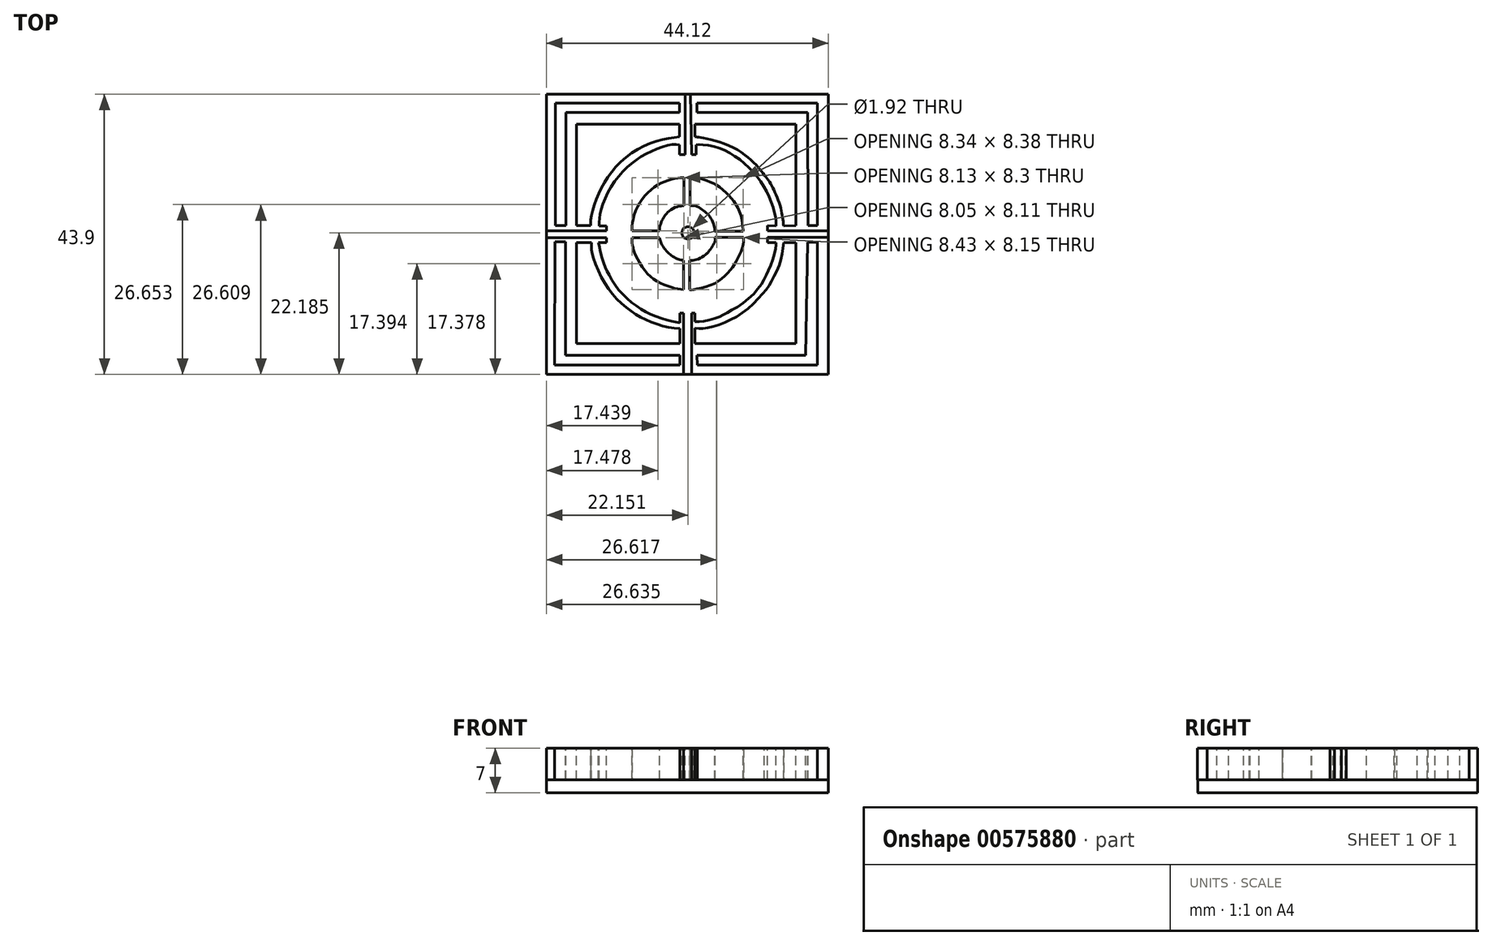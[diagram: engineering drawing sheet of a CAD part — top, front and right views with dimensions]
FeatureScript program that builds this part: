
annotation { "Feature Type Name" : "Feature", "Feature Type Description" : "" }
export const myFeature = defineFeature(function(context is Context, id is Id, definition is map)
    precondition{}
    {
        {
            var Q0;
            Q0=qCreatedBy(makeId("Top.planeOp"),FACE);
            var sketch = newSketch(context, id + "F0", { "sketchPlane" : qUnion([Q0])});
            skFitSpline(sketch, "E0", {"points": [v(14.8, 62.13) * mm, v(14.75, 42.86) * mm], "startDerivative": vector(-0.06, -19.27) * mm, "endDerivative": vector(-0.06, -19.27) * mm});
            skFitSpline(sketch, "E1", {"points": [v(14.75, 42.86) * mm, v(34.33, 42.86) * mm], "startDerivative": vector(19.6, 0) * mm, "endDerivative": vector(19.6, 0) * mm});
            skFitSpline(sketch, "E2", {"points": [v(34.33, 42.86) * mm, v(34.33, 44.38) * mm], "startDerivative": vector(0, 1.53) * mm, "endDerivative": vector(0, 1.53) * mm});
            skFitSpline(sketch, "E3", {"points": [v(34.33, 44.38) * mm, v(16.42, 44.38) * mm], "startDerivative": vector(-17.93, 0) * mm, "endDerivative": vector(-17.93, 0) * mm});
            skFitSpline(sketch, "E4", {"points": [v(16.42, 44.38) * mm, v(16.42, 62.13) * mm], "startDerivative": vector(0, 17.74) * mm, "endDerivative": vector(0, 17.74) * mm});
            skFitSpline(sketch, "E5", {"points": [v(16.42, 62.13) * mm, v(14.8, 62.13) * mm], "startDerivative": vector(-1.62, 0) * mm, "endDerivative": vector(-1.62, 0) * mm});
            skFitSpline(sketch, "E6", {"points": [v(34.33, 50.96) * mm, v(34.33, 46.2) * mm], "startDerivative": vector(0, -4.75) * mm, "endDerivative": vector(0, -4.75) * mm});
            skFitSpline(sketch, "E7", {"points": [v(34.33, 50.96) * mm, v(36.66, 50.96) * mm], "startDerivative": vector(2.34, 0) * mm, "endDerivative": vector(2.34, 0) * mm});
            skFitSpline(sketch, "E8", {"points": [v(36.66, 50.96) * mm, v(36.66, 46.2) * mm], "startDerivative": vector(0, -4.75) * mm, "endDerivative": vector(0, -4.75) * mm});
            skFitSpline(sketch, "E9", {"points": [v(34.93, 41.37) * mm, v(36.2, 41.34) * mm], "startDerivative": vector(1.22, -0.03) * mm, "endDerivative": vector(1.22, -0.03) * mm});
            skFitSpline(sketch, "E10", {"points": [v(36.2, 41.34) * mm, v(36.2, 50.96) * mm], "startDerivative": vector(0, 9.62) * mm, "endDerivative": vector(0, 9.62) * mm});
            skFitSpline(sketch, "E11", {"points": [v(34.93, 41.37) * mm, v(34.93, 50.96) * mm], "startDerivative": vector(0, 9.6) * mm, "endDerivative": vector(0, 9.6) * mm});
            skFitSpline(sketch, "E12", {"points": [v(34.33, 49.46) * mm, v(33.12, 49.7) * mm, v(30.97, 50.3) * mm, v(28.74, 51.3) * mm, v(26.75, 52.67) * mm, v(24.79, 54.57) * mm, v(23.3, 56.84) * mm, v(22.67, 58.18) * mm, v(22.03, 60.1) * mm, v(21.6, 62) * mm, v(21.6, 62.01) * mm], "startDerivative": vector(-13.94, 2.4) * mm, "endDerivative": vector(0.26, 5.24) * mm});
            skFitSpline(sketch, "E13", {"points": [v(36.66, 48.6) * mm, v(38.29, 48.6) * mm, v(41.1, 49.37) * mm, v(44.58, 51.33) * mm, v(47.54, 54.27) * mm, v(48.82, 56.2) * mm, v(50.1, 59.12) * mm, v(50.59, 62.01) * mm], "startDerivative": vector(14.49, -1.02) * mm, "endDerivative": vector(1.9, 21.32) * mm});
            skFitSpline(sketch, "E14", {"points": [v(50.59, 62.01) * mm, v(49.36, 62.01) * mm], "startDerivative": vector(-1.25, 0) * mm, "endDerivative": vector(-1.25, 0) * mm});
            skFitSpline(sketch, "E15", {"points": [v(49.36, 62.01) * mm, v(49.36, 61.46) * mm, v(48.89, 59.4) * mm, v(47.94, 57.1) * mm, v(46.93, 55.26) * mm, v(44.59, 52.79) * mm, v(41.9, 51.12) * mm, v(40.57, 50.4) * mm, v(38.37, 49.72) * mm, v(36.66, 49.61) * mm], "startDerivative": vector(0.7, -10.36) * mm, "endDerivative": vector(-15.94, 0) * mm});
            skFitSpline(sketch, "E16", {"points": [v(50.59, 64.63) * mm, v(50.2, 67.1) * mm, v(48.89, 70.6) * mm, v(47.55, 72.58) * mm], "startDerivative": vector(-0.92, 7.67) * mm, "endDerivative": vector(-5.43, 6.35) * mm});
            skFitSpline(sketch, "E17", {"points": [v(47.55, 72.58) * mm, v(46.33, 74.1) * mm, v(42.46, 77) * mm, v(37.58, 78.46) * mm, v(36.87, 78.55) * mm], "startDerivative": vector(-4.95, 6.76) * mm, "endDerivative": vector(-4.27, 0.3) * mm});
            skFitSpline(sketch, "E18", {"points": [v(36.87, 78.55) * mm, v(36.87, 77.33) * mm], "startDerivative": vector(0, -1.08) * mm, "endDerivative": vector(0, -1.08) * mm});
            skFitSpline(sketch, "E19", {"points": [v(36.87, 77.33) * mm, v(37.6, 77.33) * mm, v(39.73, 77.05) * mm, v(42.02, 76.13) * mm, v(44.29, 74.55) * mm, v(46.26, 72.58) * mm, v(47.74, 70.32) * mm, v(48.72, 68.07) * mm, v(49.31, 66.05) * mm, v(49.38, 64.63) * mm], "startDerivative": vector(9.67, 0.58) * mm, "endDerivative": vector(-0.3, -15.03) * mm});
            skFitSpline(sketch, "E20", {"points": [v(49.38, 64.63) * mm, v(50.59, 64.63) * mm], "startDerivative": vector(1.24, 0) * mm, "endDerivative": vector(1.24, 0) * mm});
            skFitSpline(sketch, "E21", {"points": [v(34.3, 77.33) * mm, v(32.9, 77.33) * mm, v(29.97, 76.37) * mm, v(27.17, 74.7) * mm, v(24.52, 72.11) * mm, v(22.5, 68.62) * mm, v(21.8, 66.05) * mm, v(21.69, 64.63) * mm], "startDerivative": vector(-12.77, 1.45) * mm, "endDerivative": vector(-0.42, -12.91) * mm});
            skFitSpline(sketch, "E22", {"points": [v(21.69, 64.63) * mm, v(20.38, 64.63) * mm], "startDerivative": vector(-1.3, 0) * mm, "endDerivative": vector(-1.3, 0) * mm});
            skFitSpline(sketch, "E23", {"points": [v(20.38, 64.63) * mm, v(20.38, 65.43) * mm, v(21.02, 68.16) * mm, v(22.78, 71.84) * mm, v(25.97, 75.45) * mm, v(30.6, 77.89) * mm, v(34.3, 78.55) * mm], "startDerivative": vector(-0.6, 8.43) * mm, "endDerivative": vector(20.4, 2.18) * mm});
            skFitSpline(sketch, "E24", {"points": [v(34.3, 78.55) * mm, v(34.3, 77.33) * mm], "startDerivative": vector(0, -1.08) * mm, "endDerivative": vector(0, -1.08) * mm});
            skFitSpline(sketch, "E25", {"points": [v(22.84, 63.84) * mm, v(22.86, 62.77) * mm], "startDerivative": vector(0.02, -1.07) * mm, "endDerivative": vector(0.02, -1.07) * mm});
            skFitSpline(sketch, "E26", {"points": [v(22.86, 62.77) * mm, v(13.46, 62.77) * mm], "startDerivative": vector(-9.4, 0) * mm, "endDerivative": vector(-9.4, 0) * mm});
            skFitSpline(sketch, "E27", {"points": [v(13.46, 62.77) * mm, v(13.46, 63.84) * mm], "startDerivative": vector(0, 1.07) * mm, "endDerivative": vector(0, 1.07) * mm});
            skFitSpline(sketch, "E28", {"points": [v(13.46, 63.84) * mm, v(22.84, 63.84) * mm], "startDerivative": vector(9.38, 0) * mm, "endDerivative": vector(9.38, 0) * mm});
            skFitSpline(sketch, "E29", {"points": [v(34.93, 52.6) * mm, v(35.89, 52.6) * mm], "startDerivative": vector(0.94, 0) * mm, "endDerivative": vector(0.94, 0) * mm});
            skFitSpline(sketch, "E30", {"points": [v(35.89, 52.6) * mm, v(35.89, 59.23) * mm], "startDerivative": vector(-0.02, 6.18) * mm, "endDerivative": vector(0, 6.62) * mm});
            skFitSpline(sketch, "E31", {"points": [v(34.93, 52.6) * mm, v(34.93, 59.23) * mm], "startDerivative": vector(0, 6.62) * mm, "endDerivative": vector(0, 6.62) * mm});
            skFitSpline(sketch, "E32", {"points": [v(34.93, 59.23) * mm, v(34.04, 59.42) * mm, v(32.96, 60) * mm, v(31.97, 61) * mm, v(31.28, 62.26) * mm, v(31.18, 62.77) * mm], "startDerivative": vector(-4.92, 0.65) * mm, "endDerivative": vector(-0.36, 3.26) * mm});
            skFitSpline(sketch, "E33", {"points": [v(31.18, 62.77) * mm, v(24.72, 62.77) * mm], "startDerivative": vector(-6.45, 0) * mm, "endDerivative": vector(-6.45, 0) * mm});
            skFitSpline(sketch, "E34", {"points": [v(24.72, 62.77) * mm, v(24.72, 63.84) * mm], "startDerivative": vector(0, 1.07) * mm, "endDerivative": vector(0, 1.07) * mm});
            skFitSpline(sketch, "E35", {"points": [v(24.72, 63.84) * mm, v(31.18, 63.84) * mm], "startDerivative": vector(6.45, 0) * mm, "endDerivative": vector(6.45, 0) * mm});
            skFitSpline(sketch, "E36", {"points": [v(35, 67.78) * mm, v(35, 74.22) * mm], "startDerivative": vector(0, 6.24) * mm, "endDerivative": vector(0, 6.24) * mm});
            skFitSpline(sketch, "E37", {"points": [v(35, 74.22) * mm, v(35.9, 74.22) * mm], "startDerivative": vector(0.93, 0) * mm, "endDerivative": vector(0.93, 0) * mm});
            skFitSpline(sketch, "E38", {"points": [v(35.9, 74.22) * mm, v(35.9, 67.78) * mm], "startDerivative": vector(0, -6.44) * mm, "endDerivative": vector(0, -6.44) * mm});
            skFitSpline(sketch, "E39", {"points": [v(31.18, 63.84) * mm, v(31.18, 64.43) * mm, v(31.6, 65.57) * mm, v(32.05, 66.33) * mm, v(33.27, 67.37) * mm, v(34.72, 67.78) * mm, v(35, 67.78) * mm], "startDerivative": vector(-0.5, 4.04) * mm, "endDerivative": vector(2.43, -0.15) * mm});
            skCircle(sketch, "E40", {"center": v(35.61, 63.53) * mm, "radius": 0.96 * mm});
            skFitSpline(sketch, "E41", {"points": [v(35.9, 67.78) * mm, v(36.73, 67.78) * mm, v(38.04, 67) * mm, v(38.94, 66.2) * mm, v(39.68, 64.68) * mm, v(39.83, 63.76) * mm], "startDerivative": vector(4.4, 0.01) * mm, "endDerivative": vector(0.37, -4.81) * mm});
            skFitSpline(sketch, "E42", {"points": [v(39.83, 63.76) * mm, v(46.25, 63.76) * mm], "startDerivative": vector(6.42, 0) * mm, "endDerivative": vector(6.42, 0) * mm});
            skFitSpline(sketch, "E43", {"points": [v(46.25, 63.76) * mm, v(46.25, 62.8) * mm], "startDerivative": vector(0, -0.95) * mm, "endDerivative": vector(0, -0.95) * mm});
            skFitSpline(sketch, "E44", {"points": [v(46.25, 62.8) * mm, v(39.83, 62.8) * mm], "startDerivative": vector(-6.42, 0) * mm, "endDerivative": vector(-6.42, 0) * mm});
            skFitSpline(sketch, "E45", {"points": [v(39.83, 62.8) * mm, v(39.83, 62.24) * mm, v(39.23, 61.11) * mm, v(38.13, 59.92) * mm, v(36.44, 59.2) * mm, v(35.89, 59.23) * mm], "startDerivative": vector(0.54, -3.65) * mm, "endDerivative": vector(-3.18, 0.59) * mm});
            skFitSpline(sketch, "E46", {"points": [v(44.3, 62.8) * mm, v(44.3, 62.07) * mm, v(43.78, 60.32) * mm, v(42.9, 58.64) * mm, v(41.5, 56.9) * mm, v(39.16, 55.34) * mm, v(36.44, 54.64) * mm, v(35.88, 54.66) * mm], "startDerivative": vector(0.66, -7) * mm, "endDerivative": vector(-5.02, 2.93) * mm});
            skFitSpline(sketch, "E47", {"points": [v(34.93, 54.66) * mm, v(33.75, 54.81) * mm, v(32.03, 55.34) * mm, v(30.18, 56.31) * mm, v(28.6, 57.96) * mm, v(27.35, 60.14) * mm, v(27.08, 60.97) * mm, v(26.87, 61.97) * mm, v(26.87, 62.77) * mm], "startDerivative": vector(-10.11, 0.86) * mm, "endDerivative": vector(0.5, 8.43) * mm});
            skFitSpline(sketch, "E48", {"points": [v(26.87, 63.84) * mm, v(26.87, 64.85) * mm, v(27.59, 67.38) * mm, v(29.28, 69.79) * mm, v(31.33, 71.28) * mm, v(33.2, 71.95) * mm, v(34.59, 72.2) * mm, v(35, 72.14) * mm], "startDerivative": vector(-0.6, 8.13) * mm, "endDerivative": vector(5.04, -1.27) * mm});
            skFitSpline(sketch, "E49", {"points": [v(35.9, 72.14) * mm, v(37.17, 72.14) * mm, v(38.93, 71.54) * mm, v(40.3, 70.85) * mm, v(41.95, 69.44) * mm, v(43.06, 68.02) * mm, v(43.97, 66.02) * mm, v(44.2, 64.3) * mm, v(44.25, 63.76) * mm], "startDerivative": vector(10.83, 1.07) * mm, "endDerivative": vector(0.71, -6.4) * mm});
            skFitSpline(sketch, "E50", {"points": [v(36.66, 46.2) * mm, v(52.53, 46.2) * mm], "startDerivative": vector(15.86, 0) * mm, "endDerivative": vector(15.86, 0) * mm});
            skFitSpline(sketch, "E51", {"points": [v(52.53, 46.2) * mm, v(52.53, 62.01) * mm], "startDerivative": vector(0, 15.8) * mm, "endDerivative": vector(0, 15.8) * mm});
            skFitSpline(sketch, "E52", {"points": [v(52.53, 62.01) * mm, v(50.59, 62.01) * mm], "startDerivative": vector(-1.96, 0) * mm, "endDerivative": vector(-1.95, 0.01) * mm});
            skFitSpline(sketch, "E53", {"points": [v(52.53, 64.67) * mm, v(50.59, 64.63) * mm], "startDerivative": vector(-1.94, -0.05) * mm, "endDerivative": vector(-1.94, -0.05) * mm});
            skFitSpline(sketch, "E54", {"points": [v(52.53, 64.67) * mm, v(52.53, 80.54) * mm], "startDerivative": vector(0, 15.87) * mm, "endDerivative": vector(0, 15.87) * mm});
            skFitSpline(sketch, "E55", {"points": [v(52.53, 80.54) * mm, v(36.66, 80.54) * mm], "startDerivative": vector(-15.86, 0) * mm, "endDerivative": vector(-15.86, 0) * mm});
            skFitSpline(sketch, "E56", {"points": [v(36.66, 80.54) * mm, v(36.66, 78.55) * mm], "startDerivative": vector(0, -2) * mm, "endDerivative": vector(0, -2) * mm});
            skFitSpline(sketch, "E57", {"points": [v(36.66, 78.55) * mm, v(36.87, 78.55) * mm], "startDerivative": vector(0.18, 0) * mm, "endDerivative": vector(0.18, 0) * mm});
            skFitSpline(sketch, "E58", {"points": [v(34.3, 80.54) * mm, v(34.3, 78.55) * mm], "startDerivative": vector(0, -2) * mm, "endDerivative": vector(0, -2) * mm});
            skFitSpline(sketch, "E59", {"points": [v(34.3, 80.54) * mm, v(18.15, 80.54) * mm], "startDerivative": vector(-16.15, 0) * mm, "endDerivative": vector(-16.15, 0) * mm});
            skFitSpline(sketch, "E60", {"points": [v(18.15, 80.54) * mm, v(18.15, 64.67) * mm], "startDerivative": vector(0, -15.87) * mm, "endDerivative": vector(0, -15.87) * mm});
            skFitSpline(sketch, "E61", {"points": [v(18.15, 64.67) * mm, v(20.38, 64.67) * mm], "startDerivative": vector(2.22, 0) * mm, "endDerivative": vector(2.22, 0) * mm});
            skFitSpline(sketch, "E62", {"points": [v(21.69, 64.63) * mm, v(22.84, 64.63) * mm], "startDerivative": vector(1.15, 0) * mm, "endDerivative": vector(1.15, 0) * mm});
            skFitSpline(sketch, "E63", {"points": [v(22.84, 64.63) * mm, v(22.84, 63.84) * mm], "startDerivative": vector(0, -0.78) * mm, "endDerivative": vector(0, -0.78) * mm});
            skFitSpline(sketch, "E64", {"points": [v(22.86, 62.77) * mm, v(22.86, 62.01) * mm], "startDerivative": vector(0, -0.76) * mm, "endDerivative": vector(0, -0.76) * mm});
            skFitSpline(sketch, "E65", {"points": [v(22.86, 62.01) * mm, v(21.6, 62) * mm], "startDerivative": vector(-1.25, -0.01) * mm, "endDerivative": vector(-1.25, -0.01) * mm});
            skFitSpline(sketch, "E66", {"points": [v(20.49, 62.03) * mm, v(18.15, 62.03) * mm], "startDerivative": vector(-2.38, 0) * mm, "endDerivative": vector(-2.38, 0) * mm});
            skFitSpline(sketch, "E67", {"points": [v(36.87, 77.33) * mm, v(36.87, 75.77) * mm], "startDerivative": vector(0, -1.7) * mm, "endDerivative": vector(0, -1.7) * mm});
            skFitSpline(sketch, "E68", {"points": [v(36.87, 75.77) * mm, v(34.3, 75.77) * mm], "startDerivative": vector(-2.56, 0) * mm, "endDerivative": vector(-2.56, 0) * mm});
            skFitSpline(sketch, "E69", {"points": [v(34.3, 75.77) * mm, v(34.3, 77.33) * mm], "startDerivative": vector(0, 1.7) * mm, "endDerivative": vector(0, 1.7) * mm});
            skFitSpline(sketch, "E70", {"points": [v(49.36, 62.01) * mm, v(48.04, 62.01) * mm], "startDerivative": vector(-1.33, 0) * mm, "endDerivative": vector(-1.33, 0) * mm});
            skFitSpline(sketch, "E71", {"points": [v(48.04, 62.01) * mm, v(48.04, 64.67) * mm], "startDerivative": vector(0, 2.41) * mm, "endDerivative": vector(0, 2.41) * mm});
            skFitSpline(sketch, "E72", {"points": [v(48.04, 64.67) * mm, v(49.38, 64.63) * mm], "startDerivative": vector(1.34, -0.05) * mm, "endDerivative": vector(1.34, -0.05) * mm});
            skFitSpline(sketch, "E73", {"points": [v(18.15, 62.03) * mm, v(18.15, 46.2) * mm], "startDerivative": vector(0, -15.81) * mm, "endDerivative": vector(0, -15.81) * mm});
            skFitSpline(sketch, "E74", {"points": [v(18.15, 46.2) * mm, v(34.33, 46.2) * mm], "startDerivative": vector(16.2, 0) * mm, "endDerivative": vector(16.2, 0) * mm});
            skFitSpline(sketch, "E75", {"points": [v(48.04, 63.87) * mm, v(57.58, 63.87) * mm], "startDerivative": vector(9.55, 0) * mm, "endDerivative": vector(9.55, 0) * mm});
            skFitSpline(sketch, "E76", {"points": [v(57.58, 63.87) * mm, v(57.58, 62.8) * mm], "startDerivative": vector(0, -1.06) * mm, "endDerivative": vector(0, -1.06) * mm});
            skFitSpline(sketch, "E77", {"points": [v(57.58, 62.8) * mm, v(48.04, 62.8) * mm], "startDerivative": vector(-9.55, 0) * mm, "endDerivative": vector(-9.55, 0) * mm});
            skFitSpline(sketch, "E78", {"points": [v(36.16, 75.77) * mm, v(36.02, 85.24) * mm], "startDerivative": vector(-0.15, 9.46) * mm, "endDerivative": vector(-0.15, 9.46) * mm});
            skFitSpline(sketch, "E79", {"points": [v(36.02, 85.24) * mm, v(35.16, 85.24) * mm], "startDerivative": vector(-0.85, 0) * mm, "endDerivative": vector(-0.85, 0) * mm});
            skFitSpline(sketch, "E80", {"points": [v(35.16, 85.24) * mm, v(35.16, 75.77) * mm], "startDerivative": vector(0, -9.46) * mm, "endDerivative": vector(0, -9.46) * mm});
            skFitSpline(sketch, "E81", {"points": [v(37.01, 44.38) * mm, v(37.04, 42.86) * mm], "startDerivative": vector(0.03, -1.53) * mm, "endDerivative": vector(0.03, -1.53) * mm});
            skFitSpline(sketch, "E82", {"points": [v(37.04, 42.86) * mm, v(55.9, 42.86) * mm], "startDerivative": vector(18.85, 0) * mm, "endDerivative": vector(18.85, 0) * mm});
            skFitSpline(sketch, "E83", {"points": [v(55.9, 42.86) * mm, v(55.9, 62.09) * mm], "startDerivative": vector(0, 19.23) * mm, "endDerivative": vector(0, 19.23) * mm});
            skFitSpline(sketch, "E84", {"points": [v(55.9, 62.09) * mm, v(54.34, 62.09) * mm], "startDerivative": vector(-1.56, 0) * mm, "endDerivative": vector(-1.56, 0) * mm});
            skFitSpline(sketch, "E85", {"points": [v(54.34, 62.09) * mm, v(54.02, 44.38) * mm], "startDerivative": vector(-0.32, -17.7) * mm, "endDerivative": vector(-0.32, -17.7) * mm});
            skFitSpline(sketch, "E86", {"points": [v(54.02, 44.38) * mm, v(37.01, 44.38) * mm], "startDerivative": vector(-17, 0) * mm, "endDerivative": vector(-17, 0) * mm});
            skFitSpline(sketch, "E87", {"points": [v(54.4, 64.64) * mm, v(55.89, 64.66) * mm], "startDerivative": vector(1.49, 0.02) * mm, "endDerivative": vector(1.49, 0.02) * mm});
            skFitSpline(sketch, "E88", {"points": [v(55.89, 64.66) * mm, v(55.89, 83.84) * mm], "startDerivative": vector(0, 19.18) * mm, "endDerivative": vector(0, 19.18) * mm});
            skFitSpline(sketch, "E89", {"points": [v(55.89, 83.84) * mm, v(37.02, 83.84) * mm], "startDerivative": vector(-18.87, 0) * mm, "endDerivative": vector(-18.87, 0) * mm});
            skFitSpline(sketch, "E90", {"points": [v(37.02, 83.84) * mm, v(37.02, 82.38) * mm], "startDerivative": vector(0, -1.46) * mm, "endDerivative": vector(0, -1.46) * mm});
            skFitSpline(sketch, "E91", {"points": [v(37.02, 82.38) * mm, v(54.34, 82.38) * mm], "startDerivative": vector(17.31, 0) * mm, "endDerivative": vector(17.31, 0) * mm});
            skFitSpline(sketch, "E92", {"points": [v(54.34, 82.38) * mm, v(54.4, 64.64) * mm], "startDerivative": vector(0.07, -17.74) * mm, "endDerivative": vector(0.07, -17.74) * mm});
            skFitSpline(sketch, "E93", {"points": [v(34.3, 82.38) * mm, v(34.25, 83.84) * mm], "startDerivative": vector(-0.04, 1.46) * mm, "endDerivative": vector(-0.04, 1.46) * mm});
            skFitSpline(sketch, "E94", {"points": [v(34.25, 83.84) * mm, v(14.82, 83.84) * mm], "startDerivative": vector(-19.43, 0) * mm, "endDerivative": vector(-19.43, 0) * mm});
            skFitSpline(sketch, "E95", {"points": [v(14.82, 83.84) * mm, v(14.82, 64.64) * mm], "startDerivative": vector(0, -19.2) * mm, "endDerivative": vector(0, -19.2) * mm});
            skFitSpline(sketch, "E96", {"points": [v(14.82, 64.64) * mm, v(16.48, 64.64) * mm], "startDerivative": vector(1.66, 0) * mm, "endDerivative": vector(1.66, 0) * mm});
            skFitSpline(sketch, "E97", {"points": [v(16.48, 64.64) * mm, v(16.48, 82.38) * mm], "startDerivative": vector(0, 17.74) * mm, "endDerivative": vector(0, 17.74) * mm});
            skFitSpline(sketch, "E98", {"points": [v(16.48, 82.38) * mm, v(34.3, 82.38) * mm], "startDerivative": vector(17.82, 0) * mm, "endDerivative": vector(17.82, 0) * mm});
            skFitSpline(sketch, "E99", {"points": [v(20.49, 62.03) * mm, v(21.6, 62) * mm], "startDerivative": vector(1.07, -0.02) * mm, "endDerivative": vector(1.07, -0.02) * mm});
            skFitSpline(sketch, "E100", {"points": [v(20.49, 62.03) * mm, v(20.49, 60.94) * mm, v(20.87, 59.43) * mm, v(22.36, 56) * mm, v(24.45, 53.2) * mm, v(26.8, 51.22) * mm, v(28.98, 49.93) * mm, v(31.78, 48.92) * mm, v(34.33, 48.55) * mm], "startDerivative": vector(-0.68, -13.26) * mm, "endDerivative": vector(19.93, -1.96) * mm});
            skSolve(sketch);
        }
        {
            var Q0;
            Q0=makeQuery(id+"F0.imprint","IMPRINT",FACE,{"disambiguationData":[TD([[makeQuery(id+"F0.imprint","IMPRINT",EDGE,{"derivedFrom":sQuery(id+"F0.wireOp",EDGE,"E0")}),1.0]])]});
            var Q1;
            Q1=makeQuery(id+"F0.imprint","IMPRINT",FACE,{"disambiguationData":[TD([[makeQuery(id+"F0.imprint","IMPRINT",EDGE,{"derivedFrom":sQuery(id+"F0.wireOp",EDGE,"E81")}),1.0]])]});
            var Q2;
            Q2=makeQuery(id+"F0.imprint","IMPRINT",FACE,{"disambiguationData":[TD([[makeQuery(id+"F0.imprint","IMPRINT",EDGE,{"derivedFrom":sQuery(id+"F0.wireOp",EDGE,"E87")}),1.0]])]});
            var Q3;
            Q3=makeQuery(id+"F0.imprint","IMPRINT",FACE,{"disambiguationData":[TD([[makeQuery(id+"F0.imprint","IMPRINT",EDGE,{"derivedFrom":sQuery(id+"F0.wireOp",EDGE,"E93")}),1.0]])]});
            var Q4;
            Q4=makeQuery(id+"F0.imprint","IMPRINT",FACE,{"disambiguationData":[TD([[makeQuery(id+"F0.imprint","IMPRINT",EDGE,{"derivedFrom":sQuery(id+"F0.wireOp",EDGE,"E66")}),1.0]])]});
            var Q5;
            Q5=makeQuery(id+"F0.imprint","IMPRINT",FACE,{"disambiguationData":[TD([[makeQuery(id+"F0.imprint","IMPRINT",EDGE,{"derivedFrom":sQuery(id+"F0.wireOp",EDGE,"E9")}),1.0]])]});
            var Q6;
            {var subQ0=sQuery(id+"F0.wireOp",EDGE,"E50");Q6=makeQuery(id+"F0.imprint","IMPRINT",FACE,{"disambiguationData":[TD([[makeQuery(id+"F0.imprint","IMPRINT",EDGE,{"derivedFrom":subQ0}),1.0]])]});}
            var Q7;
            Q7=makeQuery(id+"F0.imprint","IMPRINT",FACE,{"disambiguationData":[TD([[makeQuery(id+"F0.imprint","IMPRINT",EDGE,{"derivedFrom":sQuery(id+"F0.wireOp",EDGE,"E16")}),-1.0]])]});
            var Q8;
            {var subQ0=sQuery(id+"F0.wireOp",EDGE,"E58");Q8=makeQuery(id+"F0.imprint","IMPRINT",FACE,{"disambiguationData":[TD([[makeQuery(id+"F0.imprint","IMPRINT",EDGE,{"derivedFrom":subQ0}),-1.0]])]});}
            var Q9;
            Q9=makeQuery(id+"F0.imprint","IMPRINT",FACE,{"disambiguationData":[TD([[makeQuery(id+"F0.imprint","IMPRINT",EDGE,{"derivedFrom":sQuery(id+"F0.wireOp",EDGE,"E25")}),-1.0]])]});
            var Q10;
            {var subQ0=sQuery(id+"F0.wireOp",EDGE,"E78");Q10=makeQuery(id+"F0.imprint","IMPRINT",FACE,{"disambiguationData":[TD([[makeQuery(id+"F0.imprint","IMPRINT",EDGE,{"derivedFrom":subQ0}),1.0]])]});}
            var Q11;
            {var subQ0=sQuery(id+"F0.wireOp",EDGE,"E75");Q11=makeQuery(id+"F0.imprint","IMPRINT",FACE,{"disambiguationData":[TD([[makeQuery(id+"F0.imprint","IMPRINT",EDGE,{"derivedFrom":subQ0}),-1.0]])]});}
            var Q12;
            {var subQ7=sQuery(id+"F0.wireOp",EDGE,"E15");Q12=makeQuery(id+"F0.imprint","IMPRINT",FACE,{"disambiguationData":[TD([[makeQuery(id+"F0.imprint","IMPRINT",EDGE,{"derivedFrom":subQ7}),-1.0]])]});}
            var Q13;
            {var subQ15=sQuery(id+"F0.wireOp",EDGE,"E29");Q13=makeQuery(id+"F0.imprint","IMPRINT",FACE,{"disambiguationData":[TD([[makeQuery(id+"F0.imprint","IMPRINT",EDGE,{"derivedFrom":subQ15}),1.0]])]});}
            extrude(context, id + "F1", {"entities" : qUnion([Q0, Q1, Q2, Q3, Q4, Q5, Q6, Q7, Q8, Q9, Q10, Q11, Q12, Q13]), "oppositeDirection" : true, "depth" : 5 * mm, "offsetDistance" : 25 * mm});
        }
        {
            var Q0;
            Q0=makeQuery(id+"F1.opExtrude","CAP_FACE",FACE,{"disambiguationData":[OSD([sQuery(id+"F0.wireOp",EDGE,"E6"),sQuery(id+"F0.wireOp",EDGE,"E7"),sQuery(id+"F0.wireOp",EDGE,"E8"),sQuery(id+"F0.wireOp",EDGE,"E9"),sQuery(id+"F0.wireOp",EDGE,"E10"),sQuery(id+"F0.wireOp",EDGE,"E11"),sQuery(id+"F0.wireOp",EDGE,"E13"),sQuery(id+"F0.wireOp",EDGE,"E14"),sQuery(id+"F0.wireOp",EDGE,"E18"),sQuery(id+"F0.wireOp",EDGE,"E20"),sQuery(id+"F0.wireOp",EDGE,"E22"),sQuery(id+"F0.wireOp",EDGE,"E23"),sQuery(id+"F0.wireOp",EDGE,"E24"),sQuery(id+"F0.wireOp",EDGE,"E26"),sQuery(id+"F0.wireOp",EDGE,"E27"),sQuery(id+"F0.wireOp",EDGE,"E28"),sQuery(id+"F0.wireOp",EDGE,"E30"),sQuery(id+"F0.wireOp",EDGE,"E31"),sQuery(id+"F0.wireOp",EDGE,"E32"),sQuery(id+"F0.wireOp",EDGE,"E33"),sQuery(id+"F0.wireOp",EDGE,"E35"),sQuery(id+"F0.wireOp",EDGE,"E36"),sQuery(id+"F0.wireOp",EDGE,"E38"),sQuery(id+"F0.wireOp",EDGE,"E39"),sQuery(id+"F0.wireOp",EDGE,"E40"),sQuery(id+"F0.wireOp",EDGE,"E41"),sQuery(id+"F0.wireOp",EDGE,"E42"),sQuery(id+"F0.wireOp",EDGE,"E44"),sQuery(id+"F0.wireOp",EDGE,"E45"),sQuery(id+"F0.wireOp",EDGE,"E46"),sQuery(id+"F0.wireOp",EDGE,"E47"),sQuery(id+"F0.wireOp",EDGE,"E48"),sQuery(id+"F0.wireOp",EDGE,"E49"),sQuery(id+"F0.wireOp",EDGE,"E50"),sQuery(id+"F0.wireOp",EDGE,"E51"),sQuery(id+"F0.wireOp",EDGE,"E52"),sQuery(id+"F0.wireOp",EDGE,"E53"),sQuery(id+"F0.wireOp",EDGE,"E54"),sQuery(id+"F0.wireOp",EDGE,"E55"),sQuery(id+"F0.wireOp",EDGE,"E56"),sQuery(id+"F0.wireOp",EDGE,"E57"),sQuery(id+"F0.wireOp",EDGE,"E58"),sQuery(id+"F0.wireOp",EDGE,"E59"),sQuery(id+"F0.wireOp",EDGE,"E60"),sQuery(id+"F0.wireOp",EDGE,"E61"),sQuery(id+"F0.wireOp",EDGE,"E62"),sQuery(id+"F0.wireOp",EDGE,"E63"),sQuery(id+"F0.wireOp",EDGE,"E64"),sQuery(id+"F0.wireOp",EDGE,"E65"),sQuery(id+"F0.wireOp",EDGE,"E66"),sQuery(id+"F0.wireOp",EDGE,"E67"),sQuery(id+"F0.wireOp",EDGE,"E68"),sQuery(id+"F0.wireOp",EDGE,"E69"),sQuery(id+"F0.wireOp",EDGE,"E70"),sQuery(id+"F0.wireOp",EDGE,"E71"),sQuery(id+"F0.wireOp",EDGE,"E72"),sQuery(id+"F0.wireOp",EDGE,"E73"),sQuery(id+"F0.wireOp",EDGE,"E74"),sQuery(id+"F0.wireOp",EDGE,"E75"),sQuery(id+"F0.wireOp",EDGE,"E76"),sQuery(id+"F0.wireOp",EDGE,"E77"),sQuery(id+"F0.wireOp",EDGE,"E78"),sQuery(id+"F0.wireOp",EDGE,"E79"),sQuery(id+"F0.wireOp",EDGE,"E80"),sQuery(id+"F0.wireOp",EDGE,"E99")])],"isStart":false});
            var sketch = newSketch(context, id + "F2", { "sketchPlane" : qUnion([Q0])});
            skLineSegment(sketch, "E101", {"start": v(36.2, -41.34) * mm, "end": v(57.58, -41.37) * mm});
            skLineSegment(sketch, "E102", {"start": v(57.58, -41.37) * mm, "end": v(57.58, -85.24) * mm});
            skLineSegment(sketch, "E103", {"start": v(13.46, -85.24) * mm, "end": v(57.58, -85.24) * mm});
            skLineSegment(sketch, "E104", {"start": v(13.46, -85.24) * mm, "end": v(13.46, -41.37) * mm});
            skLineSegment(sketch, "E105", {"start": v(36.2, -41.34) * mm, "end": v(13.46, -41.37) * mm});
            skSolve(sketch);
        }
        {
            var Q0;
            Q0=qSketchRegion(id+"F2",true);
            extrude(context, id + "F3", {"entities" : qUnion([Q0]), "depth" : 2 * mm, "offsetDistance" : 25 * mm});
        }
    });
